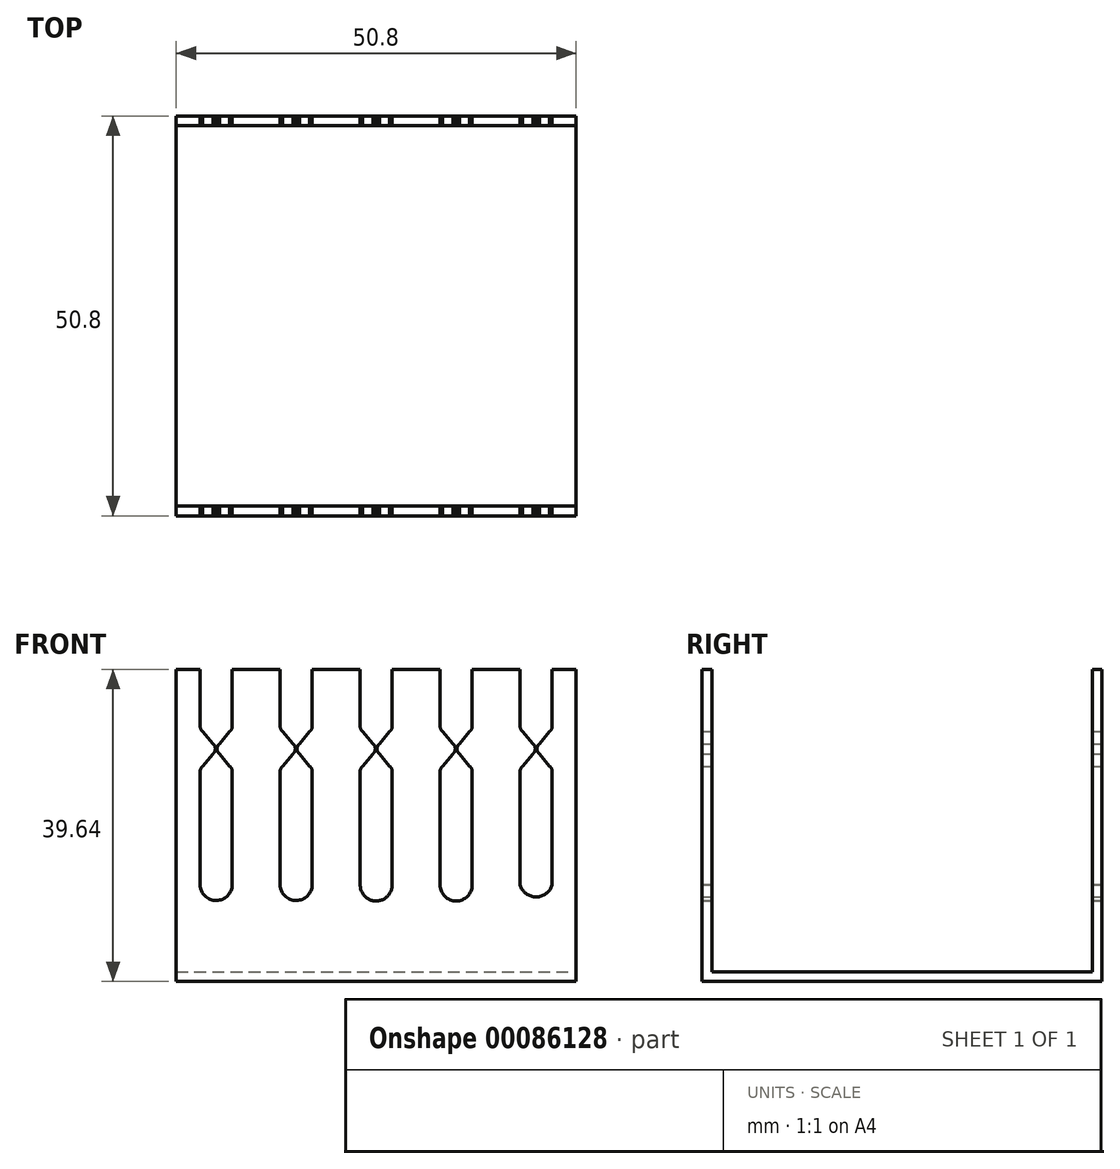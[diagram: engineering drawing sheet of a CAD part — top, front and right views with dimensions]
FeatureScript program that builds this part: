
annotation { "Feature Type Name" : "Feature", "Feature Type Description" : "" }
export const myFeature = defineFeature(function(context is Context, id is Id, definition is map)
    precondition{}
    {
        {
            var Q0;
            Q0=qCreatedBy(makeId("Front.planeOp"),FACE);
            var sketch = newSketch(context, id + "F0", { "sketchPlane" : qUnion([Q0])});
            skLineSegment(sketch, "E0", {"start": v(12.2, 18.95) * mm, "end": v(12.2, 11.7) * mm});
            skLineSegment(sketch, "E1", {"start": v(18.29, 18.95) * mm, "end": v(18.29, 11.7) * mm});
            skLineSegment(sketch, "E2", {"start": v(10.58, 9.5) * mm, "end": v(11.87, 11.06) * mm});
            skLineSegment(sketch, "E3", {"start": v(12.2, 6.02) * mm, "end": v(12.2, -8.43) * mm});
            skArc(sketch, "E4", {"start": v(11.87, 11.06) * mm, "mid": v(12.1, 11.34) * mm, "end": v(12.2, 11.7) * mm});
            skLineSegment(sketch, "E5", {"start": v(10.58, 8.22) * mm, "end": v(11.87, 6.66) * mm});
            skArc(sketch, "E6", {"start": v(12.2, 6.02) * mm, "mid": v(12.1, 6.38) * mm, "end": v(11.87, 6.66) * mm});
            skArc(sketch, "E7", {"start": v(10.58, 9.5) * mm, "mid": v(10.27, 8.86) * mm, "end": v(10.58, 8.22) * mm});
            skArc(sketch, "E8", {"start": v(19.9, 8.22) * mm, "mid": v(20.21, 8.86) * mm, "end": v(19.9, 9.5) * mm});
            skLineSegment(sketch, "E9", {"start": v(19.9, 8.22) * mm, "end": v(18.6, 6.66) * mm});
            skArc(sketch, "E10", {"start": v(18.6, 6.66) * mm, "mid": v(18.37, 6.38) * mm, "end": v(18.29, 6.02) * mm});
            skLineSegment(sketch, "E11", {"start": v(19.9, 9.5) * mm, "end": v(18.6, 11.06) * mm});
            skArc(sketch, "E12", {"start": v(18.29, 11.7) * mm, "mid": v(18.37, 11.34) * mm, "end": v(18.6, 11.06) * mm});
            skLineSegment(sketch, "E13", {"start": v(8.13, 6.02) * mm, "end": v(8.13, -8.43) * mm});
            skLineSegment(sketch, "E14", {"start": v(2.03, 6.02) * mm, "end": v(2.03, -8.37) * mm});
            skArc(sketch, "E15", {"start": v(0.42, 9.5) * mm, "mid": v(0.1, 8.86) * mm, "end": v(0.42, 8.22) * mm});
            skArc(sketch, "E16", {"start": v(9.74, 8.22) * mm, "mid": v(10.05, 8.86) * mm, "end": v(9.74, 9.5) * mm});
            skLineSegment(sketch, "E17", {"start": v(9.74, 8.22) * mm, "end": v(8.45, 6.66) * mm});
            skArc(sketch, "E18", {"start": v(8.45, 6.66) * mm, "mid": v(8.21, 6.38) * mm, "end": v(8.13, 6.02) * mm});
            skArc(sketch, "E19", {"start": v(2.03, 6.02) * mm, "mid": v(1.95, 6.38) * mm, "end": v(1.71, 6.66) * mm});
            skLineSegment(sketch, "E20", {"start": v(0.42, 8.22) * mm, "end": v(1.71, 6.66) * mm});
            skLineSegment(sketch, "E21", {"start": v(8.13, 18.95) * mm, "end": v(8.13, 11.7) * mm});
            skLineSegment(sketch, "E22", {"start": v(9.74, 9.5) * mm, "end": v(8.45, 11.06) * mm});
            skArc(sketch, "E23", {"start": v(8.13, 11.7) * mm, "mid": v(8.21, 11.34) * mm, "end": v(8.45, 11.06) * mm});
            skLineSegment(sketch, "E24", {"start": v(2.03, 18.95) * mm, "end": v(2.03, 11.7) * mm});
            skArc(sketch, "E25", {"start": v(1.71, 11.06) * mm, "mid": v(1.95, 11.34) * mm, "end": v(2.03, 11.7) * mm});
            skLineSegment(sketch, "E26", {"start": v(0.42, 9.5) * mm, "end": v(1.71, 11.06) * mm});
            skLineSegment(sketch, "E27", {"start": v(-8.13, 6.02) * mm, "end": v(-8.13, -8.37) * mm});
            skLineSegment(sketch, "E28", {"start": v(-2.03, 6.02) * mm, "end": v(-2.03, -8.43) * mm});
            skArc(sketch, "E29", {"start": v(-9.74, 9.5) * mm, "mid": v(-10.05, 8.86) * mm, "end": v(-9.74, 8.22) * mm});
            skLineSegment(sketch, "E30", {"start": v(-9.74, 8.22) * mm, "end": v(-8.45, 6.66) * mm});
            skArc(sketch, "E31", {"start": v(-8.13, 6.02) * mm, "mid": v(-8.21, 6.38) * mm, "end": v(-8.45, 6.66) * mm});
            skLineSegment(sketch, "E32", {"start": v(-8.13, 18.95) * mm, "end": v(-8.13, 11.7) * mm});
            skLineSegment(sketch, "E33", {"start": v(-9.74, 9.5) * mm, "end": v(-8.45, 11.06) * mm});
            skArc(sketch, "E34", {"start": v(-8.45, 11.06) * mm, "mid": v(-8.21, 11.34) * mm, "end": v(-8.13, 11.7) * mm});
            skLineSegment(sketch, "E35", {"start": v(-0.42, 8.22) * mm, "end": v(-1.71, 6.66) * mm});
            skArc(sketch, "E36", {"start": v(-1.71, 6.66) * mm, "mid": v(-1.95, 6.38) * mm, "end": v(-2.03, 6.02) * mm});
            skLineSegment(sketch, "E37", {"start": v(-2.03, 18.95) * mm, "end": v(-2.03, 11.7) * mm});
            skLineSegment(sketch, "E38", {"start": v(-0.42, 9.5) * mm, "end": v(-1.71, 11.06) * mm});
            skArc(sketch, "E39", {"start": v(-2.03, 11.7) * mm, "mid": v(-1.95, 11.34) * mm, "end": v(-1.71, 11.06) * mm});
            skArc(sketch, "E40", {"start": v(-0.42, 8.22) * mm, "mid": v(-0.1, 8.86) * mm, "end": v(-0.42, 9.5) * mm});
            skLineSegment(sketch, "E41", {"start": v(-18.29, 6.02) * mm, "end": v(-18.29, -8.37) * mm});
            skLineSegment(sketch, "E42", {"start": v(-12.2, 6.02) * mm, "end": v(-12.2, -8.43) * mm});
            skArc(sketch, "E43", {"start": v(-19.9, 9.5) * mm, "mid": v(-20.21, 8.86) * mm, "end": v(-19.9, 8.22) * mm});
            skLineSegment(sketch, "E44", {"start": v(-19.9, 8.22) * mm, "end": v(-18.6, 6.66) * mm});
            skArc(sketch, "E45", {"start": v(-18.29, 6.02) * mm, "mid": v(-18.37, 6.38) * mm, "end": v(-18.6, 6.66) * mm});
            skLineSegment(sketch, "E46", {"start": v(-18.29, 18.95) * mm, "end": v(-18.29, 11.7) * mm});
            skLineSegment(sketch, "E47", {"start": v(-19.9, 9.5) * mm, "end": v(-18.6, 11.06) * mm});
            skArc(sketch, "E48", {"start": v(-18.6, 11.06) * mm, "mid": v(-18.37, 11.34) * mm, "end": v(-18.29, 11.7) * mm});
            skLineSegment(sketch, "E49", {"start": v(-10.58, 8.22) * mm, "end": v(-11.87, 6.66) * mm});
            skArc(sketch, "E50", {"start": v(-11.87, 6.66) * mm, "mid": v(-12.1, 6.38) * mm, "end": v(-12.2, 6.02) * mm});
            skLineSegment(sketch, "E51", {"start": v(-12.2, 18.95) * mm, "end": v(-12.2, 11.7) * mm});
            skLineSegment(sketch, "E52", {"start": v(-10.58, 9.5) * mm, "end": v(-11.87, 11.06) * mm});
            skArc(sketch, "E53", {"start": v(-12.2, 11.7) * mm, "mid": v(-12.1, 11.34) * mm, "end": v(-11.87, 11.06) * mm});
            skArc(sketch, "E54", {"start": v(-10.58, 8.22) * mm, "mid": v(-10.27, 8.86) * mm, "end": v(-10.58, 9.5) * mm});
            skLineSegment(sketch, "E55", {"start": v(-22.35, 6.02) * mm, "end": v(-22.35, -8.43) * mm});
            skLineSegment(sketch, "E56", {"start": v(-20.74, 8.22) * mm, "end": v(-22.03, 6.66) * mm});
            skArc(sketch, "E57", {"start": v(-22.03, 6.66) * mm, "mid": v(-22.27, 6.38) * mm, "end": v(-22.35, 6.02) * mm});
            skLineSegment(sketch, "E58", {"start": v(-22.35, 18.95) * mm, "end": v(-22.35, 11.7) * mm});
            skLineSegment(sketch, "E59", {"start": v(-20.74, 9.5) * mm, "end": v(-22.03, 11.06) * mm});
            skArc(sketch, "E60", {"start": v(-22.35, 11.7) * mm, "mid": v(-22.27, 11.34) * mm, "end": v(-22.03, 11.06) * mm});
            skArc(sketch, "E61", {"start": v(-20.74, 8.22) * mm, "mid": v(-20.43, 8.86) * mm, "end": v(-20.74, 9.5) * mm});
            skArc(sketch, "E62", {"start": v(18.29, -8.43) * mm, "mid": v(20.32, -9.95) * mm, "end": v(22.35, -8.43) * mm});
            skLineSegment(sketch, "E63", {"start": v(20.74, 8.22) * mm, "end": v(22.03, 6.66) * mm});
            skArc(sketch, "E64", {"start": v(22.35, 6.02) * mm, "mid": v(22.27, 6.38) * mm, "end": v(22.03, 6.66) * mm});
            skLineSegment(sketch, "E65", {"start": v(22.35, 18.95) * mm, "end": v(22.35, 11.7) * mm});
            skLineSegment(sketch, "E66", {"start": v(20.74, 9.5) * mm, "end": v(22.03, 11.06) * mm});
            skArc(sketch, "E67", {"start": v(22.03, 11.06) * mm, "mid": v(22.27, 11.34) * mm, "end": v(22.35, 11.7) * mm});
            skArc(sketch, "E68", {"start": v(20.74, 9.5) * mm, "mid": v(20.43, 8.86) * mm, "end": v(20.74, 8.22) * mm});
            skLineSegment(sketch, "E69", {"start": v(25.4, 18.95) * mm, "end": v(25.4, -20.69) * mm});
            skLineSegment(sketch, "E70", {"start": v(25.4, -20.69) * mm, "end": v(-25.4, -20.69) * mm});
            skLineSegment(sketch, "E71", {"start": v(-25.4, -20.69) * mm, "end": v(-25.4, 18.95) * mm});
            skLineSegment(sketch, "E72", {"start": v(25.4, 18.95) * mm, "end": v(22.35, 18.95) * mm});
            skLineSegment(sketch, "E73.trimOffspring", {"start": v(-22.35, 18.95) * mm, "end": v(-25.4, 18.95) * mm});
            skLineSegment(sketch, "E74.trimOffspring", {"start": v(-12.2, 18.95) * mm, "end": v(-18.29, 18.95) * mm});
            skLineSegment(sketch, "E75.trimOffspring", {"start": v(-2.03, 18.95) * mm, "end": v(-8.13, 18.95) * mm});
            skLineSegment(sketch, "E76.trimOffspring", {"start": v(8.13, 18.95) * mm, "end": v(2.03, 18.95) * mm});
            skArc(sketch, "E77", {"start": v(-22.35, -8.43) * mm, "mid": v(-20.3, -10.4) * mm, "end": v(-18.29, -8.37) * mm});
            skArc(sketch, "E78", {"start": v(-12.2, -8.43) * mm, "mid": v(-10.13, -10.4) * mm, "end": v(-8.13, -8.37) * mm});
            skArc(sketch, "E79", {"start": v(-2.03, -8.43) * mm, "mid": v(0.03, -10.47) * mm, "end": v(2.03, -8.37) * mm});
            skArc(sketch, "E80", {"start": v(8.13, -8.43) * mm, "mid": v(10.16, -10.47) * mm, "end": v(12.2, -8.43) * mm});
            skLineSegment(sketch, "E81", {"start": v(18.29, -8.43) * mm, "end": v(18.29, 6.02) * mm});
            skLineSegment(sketch, "E82", {"start": v(22.35, 6.02) * mm, "end": v(22.35, -8.43) * mm});
            skLineSegment(sketch, "E83", {"start": v(18.29, 18.95) * mm, "end": v(12.2, 18.95) * mm});
            skSolve(sketch);
        }
        {
            var Q0;
            Q0=makeQuery(id+"F0.imprint","IMPRINT",FACE,{"disambiguationData":[TD([[makeQuery(id+"F0.imprint","IMPRINT",EDGE,{"derivedFrom":sQuery(id+"F0.wireOp",EDGE,"E0")}),1.0]])]});
            extrude(context, id + "F1", {"entities" : qUnion([Q0]), "depth" : 50.8 * mm});
        }
        {
            var Q0;
            Q0=makeQuery(id+"F1.opExtrude","SWEPT_FACE",FACE,{"disambiguationData":[OSD([sQuery(id+"F0.wireOp",EDGE,"E69")])]});
            var sketch = newSketch(context, id + "F2", { "sketchPlane" : qUnion([Q0])});
            skLineSegment(sketch, "E84.bottom", {"start": v(-50.8, -20.7) * mm, "end": v(0, -20.7) * mm});
            skLineSegment(sketch, "E84.top", {"start": v(-50.8, 19) * mm, "end": v(-49.54, 19) * mm});
            skLineSegment(sketch, "E84.left", {"start": v(-50.8, -20.7) * mm, "end": v(-50.8, 19) * mm});
            skLineSegment(sketch, "E84.right", {"start": v(0, -20.7) * mm, "end": v(0, 19) * mm});
            skLineSegment(sketch, "E85.0", {"start": v(-49.54, -19.48) * mm, "end": v(-49.54, 21.16) * mm});
            skLineSegment(sketch, "E85.1", {"start": v(-49.59, -19.48) * mm, "end": v(-1.22, -19.48) * mm});
            skLineSegment(sketch, "E85.2", {"start": v(-1.22, -19.48) * mm, "end": v(-1.22, 21.16) * mm});
            skLineSegment(sketch, "E86", {"start": v(-49.54, 21.16) * mm, "end": v(-1.22, 21.16) * mm});
            skLineSegment(sketch, "E87.trimOffspring", {"start": v(-1.22, 19) * mm, "end": v(0, 19) * mm});
            skSolve(sketch);
        }
        {
            var Q0;
            {var subQ0=sQuery(id+"F2.wireOp",EDGE,"E85.1");var subQ1=sQuery(id+"F2.wireOp",EDGE,"E85.0");var subQ2=makeQuery(id+"F2.imprint","INTERSECT",VERTEX,{"derivedFrom":[subQ1,subQ0]});Q0=makeQuery(id+"F2.imprint","IMPRINT",FACE,{"disambiguationData":[TD([[makeQuery(id+"F2.imprint","IMPRINT",EDGE,{"disambiguationData":[TD([[subQ2,-1.0]])],"derivedFrom":subQ0}),1.0]])]});}
            extrude(context, id + "F3", {"entities" : qUnion([Q0]), "operationType" : NewBodyOperationType.REMOVE, "oppositeDirection" : true, "depth" : 107.43 * mm});
        }
    });
